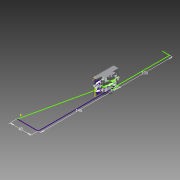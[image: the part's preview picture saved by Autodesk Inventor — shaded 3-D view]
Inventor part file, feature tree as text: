
AUTODESK INVENTOR PART (.ipt)
format: ipt  version: 2015 (Build 190159000, 159)  size: 180,224 bytes
history: native  units: in
note: dims shown in document units (in); Inventor stores cm internally (conversion verified against a paired STEP export)
features: extrude x7, sketch x2
ambient origin geometry x8: Origin, YZ Plane, XZ Plane, XY Plane, X Axis, Y Axis, Z Axis, Center Point
bodies: Body1 (feature_tree)
feature tree (9):
  extrude  "Extrusion4"  Depth=0.1181in
  extrude  "Extrusion5"  Depth=0.1181in
  extrude  "Extrusion6"  Depth=0.3937in
  extrude  "Extrusion7"  Depth=0.3937in
  sketch  "Sketch2"  dims[d0=5.7087in d1=0.1181in]
  extrude  "Extrusion8"  Depth=0.3937in
  extrude  "Extrusion9"  Depth=0.3937in
  extrude  "Extrusion10"  Depth=0.3937in
  sketch  "Sketch3"  dims[d2=0.1969in d4=0.1181in d5=1.5748in d6=4.1339in d7=0.8661in d8=0.2362in d10=0.3937in d11=0.3937in d12=0.1969in d13=0.1969in d20=0.6693in d21=1.1024in d22=0.0in d23=0.7283in d24=0.0in d25=0.4134in d26=0.0in d27=0.374in d28=0.0in d29=0.1969in d30=0.2756in d31=0.2756in d32=0.189in d33=0.189in d34=0.315in d35=0.315in d36=0.4134in d37=0.0in d38=0.1969in d39=0.0in d40=0.1969in d41=0.2756in d42=0.2756in d43=0.189in d44=0.189in d45=0.3937in d46=0.0in]
